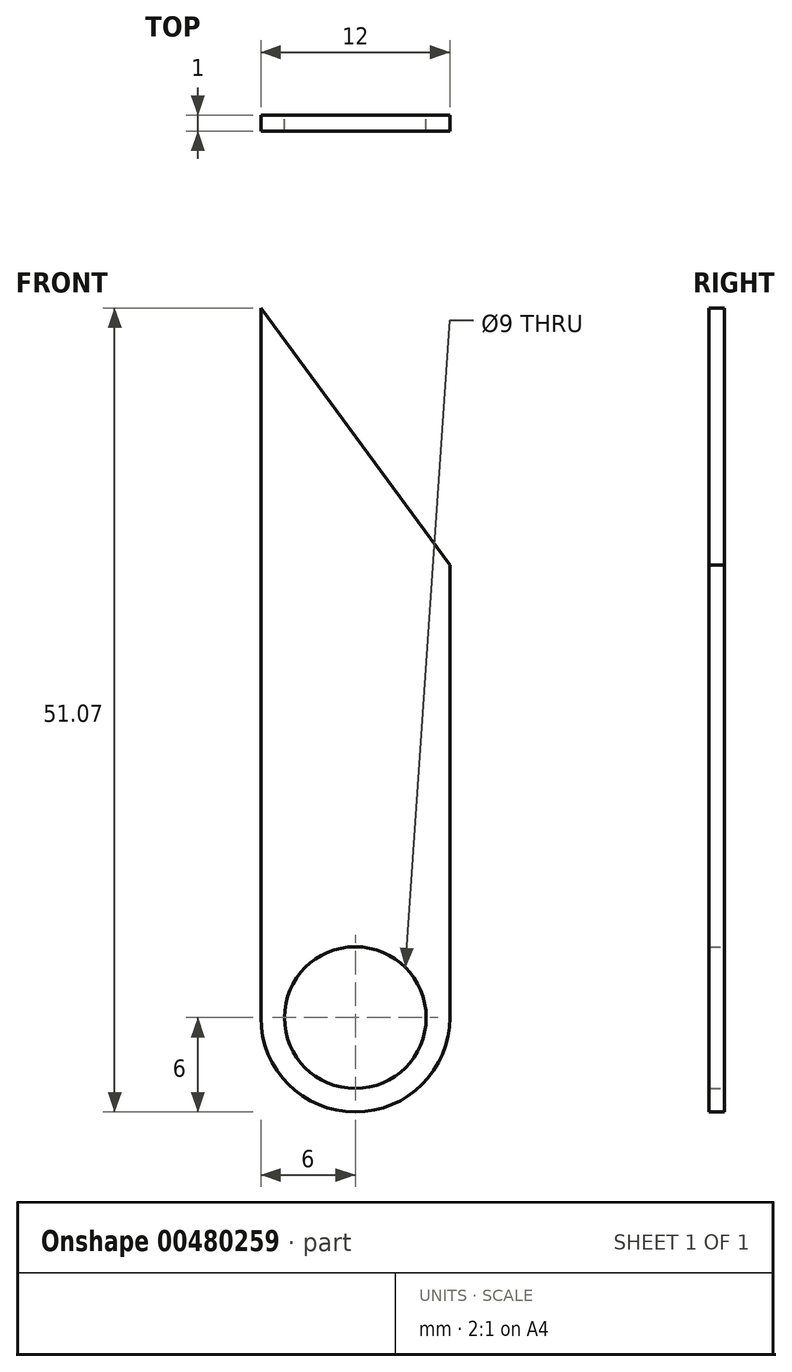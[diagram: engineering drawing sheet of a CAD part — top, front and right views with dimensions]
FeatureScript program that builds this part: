
annotation { "Feature Type Name" : "Feature", "Feature Type Description" : "" }
export const myFeature = defineFeature(function(context is Context, id is Id, definition is map)
    precondition{}
    {
        {
            var Q0;
            Q0=qCreatedBy(makeId("Front.planeOp"),FACE);
            var sketch = newSketch(context, id + "F0", { "sketchPlane" : qUnion([Q0])});
            skCircle(sketch, "E0", {"center": v(0, 0) * mm, "radius": 4.5 * mm});
            skArc(sketch, "E1", {"start": v(-6, 0) * mm, "mid": v(0, -6) * mm, "end": v(6, 0) * mm});
            skLineSegment(sketch, "E2", {"start": v(-6, 0) * mm, "end": v(-6, 45.07) * mm});
            skLineSegment(sketch, "E3", {"start": v(6, 0) * mm, "end": v(6, 28.76) * mm});
            skLineSegment(sketch, "E4", {"start": v(6, 28.76) * mm, "end": v(-6, 45.07) * mm});
            skSolve(sketch);
        }
        {
            var Q0;
            Q0 = qSketchRegion(id + "F0", true);
            extrude(context, id + "F1", {"entities" : qUnion([Q0]), "depth" : 1 * mm});
        }
    });
